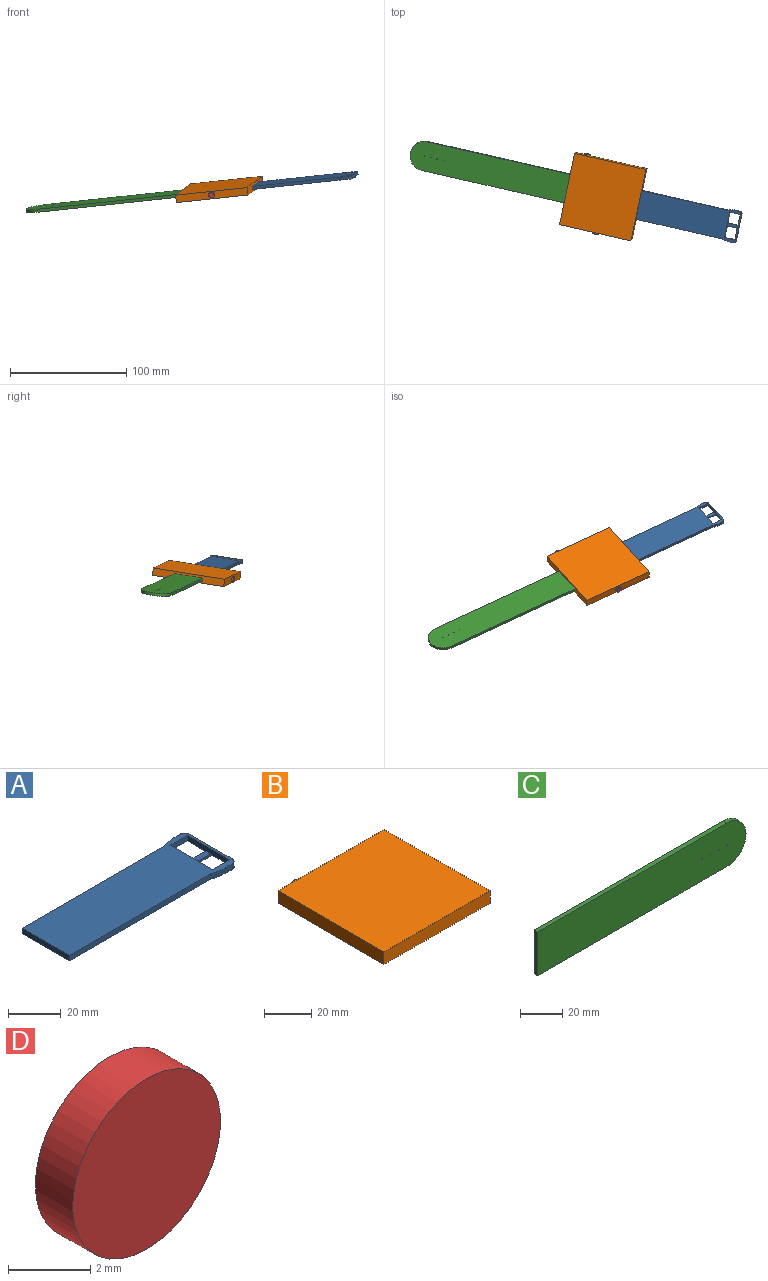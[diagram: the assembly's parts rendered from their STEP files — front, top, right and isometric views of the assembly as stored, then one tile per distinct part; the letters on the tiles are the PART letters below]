
ASSEMBLY  parts=4 mates=3
PART A: 24 faces, bbox 88.9x27.9x3.3 mm
  f0: plane 22.82x2.54mm, normal (-1,0,0), area 57.3mm2, adj f1,f2,f12,f13,f14,f15,f16
  f1: plane 88.9x27.94mm, normal (0,0,1), area 2071.9mm2, adj f0,f3,f4,f5,f6,f7,f8,f9
  f2: plane 88.9x27.94mm, normal (0,0,-1), area 2069.5mm2, adj f0,f3,f4,f5,f6,f7,f8,f9
  f3: plane 76.2x2.54mm, normal (0,-1,0), area 193.5mm2, adj f1,f2,f4,f10
  f4: plane 2.54x2.41mm, normal (-0.27,-0.96,0), area 6.4mm2, adj f1,f2,f3,f23
  f5: plane 3.33x2.54mm, normal (0,-1,0), area 8.5mm2, adj f1,f2,f20,f23
  f6: plane 22.86x2.54mm, normal (1,0,0), area 58.1mm2, adj f1,f2,f20,f21
  f7: plane 3.33x2.54mm, normal (0,1,0), area 8.5mm2, adj f1,f2,f21,f22
  f8: plane 2.54x2.41mm, normal (-0.27,0.96,0), area 6.4mm2, adj f1,f2,f9,f22
  f9: plane 76.2x2.54mm, normal (0,1,0), area 193.5mm2, adj f1,f2,f8,f10
  f10: plane 25.4x2.54mm, normal (-1,0,0), area 64.5mm2, adj f1,f2,f3,f9
  f11: plane 22.82x2.54mm, normal (1,0,0), area 57.3mm2, adj f1,f2,f12,f13,f14,f15,f16
  f12: plane 9.18x2.54mm, normal (0,1,0), area 23.3mm2, adj f0,f1,f2,f11
  f13: plane 9.18x2.54mm, normal (0,-1,0), area 23.3mm2, adj f0,f1,f2,f11
  f14: plane 10.12x1.02mm, normal (0,1,0), area 10mm2, adj f0,f2,f11,f16,f17,f18,f19
  f15: plane 10.12x1.02mm, normal (0,-1,0), area 10mm2, adj f0,f2,f11,f16,f17,f18,f19
  f16: plane 9.18x2.54mm, normal (0,0,1), area 23.3mm2, adj f0,f11,f14,f15
  f17: plane 2.54x0.76mm, normal (-1,0,0), area 1.9mm2, adj f2,f14,f15,f19
  f18: plane 2.54x0.76mm, normal (1,0,0), area 1.9mm2, adj f2,f14,f15,f19
  f19: plane 10.12x2.54mm, normal (0,0,-1), area 25.7mm2, adj f14,f15,f17,f18
  f20: cylinder r=2.54mm len=2.54mm, axis (0,0,-1), area 10.1mm2, adj f1,f2,f5,f6
  f21: cylinder r=2.54mm len=2.54mm, axis (0,0,-1), area 10.1mm2, adj f1,f2,f6,f7
  f22: cylinder r=16.51mm len=4.41mm, axis (0,0,-1), area 11.3mm2, adj f1,f2,f7,f8
  f23: cylinder r=16.51mm len=4.41mm, axis (0,0,-1), area 11.3mm2, adj f1,f2,f4,f5
PART B: 8 faces, bbox 63.5x64.8x6.5 mm
  f0: plane 63.5x6.48mm, normal (0,-1,0), area 411.3mm2, adj f1,f3,f4,f5
  f1: plane 63.5x6.48mm, normal (1,0,0), area 411.3mm2, adj f0,f2,f4,f5
  f2: plane 63.5x6.48mm, normal (0,1,0), area 391mm2, adj f1,f3,f4,f5,f6
  f3: plane 63.5x6.48mm, normal (-1,0,0), area 411.3mm2, adj f0,f2,f4,f5
  f4: plane 63.5x63.5mm, normal (0,0,1), area 4032.3mm2, adj f0,f1,f2,f3
  f5: plane 63.5x63.5mm, normal (0,0,-1), area 4032.3mm2, adj f0,f1,f2,f3
  f6: cylinder r=2.54mm len=5.08mm, axis (0,-1,0), area 21.3mm2, adj f2,f7
  f7: plane 5.08x5.08mm, normal (0,1,0), area 20.3mm2, adj f6
PART C: 10 faces, bbox 139.6x2.5x25.4 mm
  f0: cylinder r=12.7mm len=25.4mm, axis (0,1,0), area 101.3mm2, adj f1,f6,f8,f9
  f1: plane 127x2.54mm, normal (0,0,1), area 322.6mm2, adj f0,f2,f8,f9
  f2: plane 25.4x2.54mm, normal (-1,0,0), area 64.5mm2, adj f1,f6,f8,f9
  f3: cylinder r=0.25mm len=2.54mm, axis (0,1,0), area 4mm2, adj f8,f9
  f4: cylinder r=0.25mm len=2.54mm, axis (0,1,0), area 4mm2, adj f8,f9
  f5: cylinder r=0.25mm len=2.54mm, axis (0,1,0), area 4mm2, adj f8,f9
  f6: plane 126.79x2.54mm, normal (0,0,-1), area 322mm2, adj f0,f2,f8,f9
  f7: cylinder r=0.25mm len=2.54mm, axis (0,1,0), area 4mm2, adj f8,f9
  f8: plane 139.6x25.4mm, normal (0,-1,0), area 3475.7mm2, adj f0,f1,f2,f3,f4,f5,f6,f7
  f9: plane 139.6x25.4mm, normal (0,1,0), area 3475.7mm2, adj f0,f1,f2,f3,f4,f5,f6,f7
PART D: 3 faces, bbox 5.1x1.3x5.1 mm
  f0: cylinder r=2.54mm len=5.08mm, axis (0,1,0), area 20.6mm2, adj f1,f2
  f1: plane 5.08x5.08mm, normal (0,-1,0), area 20.3mm2, adj f0
  f2: plane 5.08x5.08mm, normal (0,1,0), area 20.3mm2, adj f0
PLACE A rot(axis=(0.5,-0.42,-0.76),16.3deg) t=(64.22,57.16,-31.32)mm
PLACE B rot(axis=(0.5,-0.42,-0.76),16.3deg) t=(-9.41,74.28,-41.12)mm fixed
PLACE C rot(axis=(0.03,0.65,0.76),166.4deg) t=(-70.64,87.55,-43.14)mm
PLACE D rot(axis=(0.5,-0.42,-0.76),16.3deg) t=(10.7,69.69,-38.98)mm
MATE fastened D.f0 <-> B.f0  axis (0.2,0.97,0.15) through (-16.33,43.17,-42.8)mm
MATE fastened B.f1 <-> A.f10  axis (0.97,-0.22,0.1) through (20.95,66.84,-34.66)mm
MATE fastened C.f2 <-> B.f3  axis (0.97,-0.22,0.1) through (-40.63,80.9,-41.22)mm
